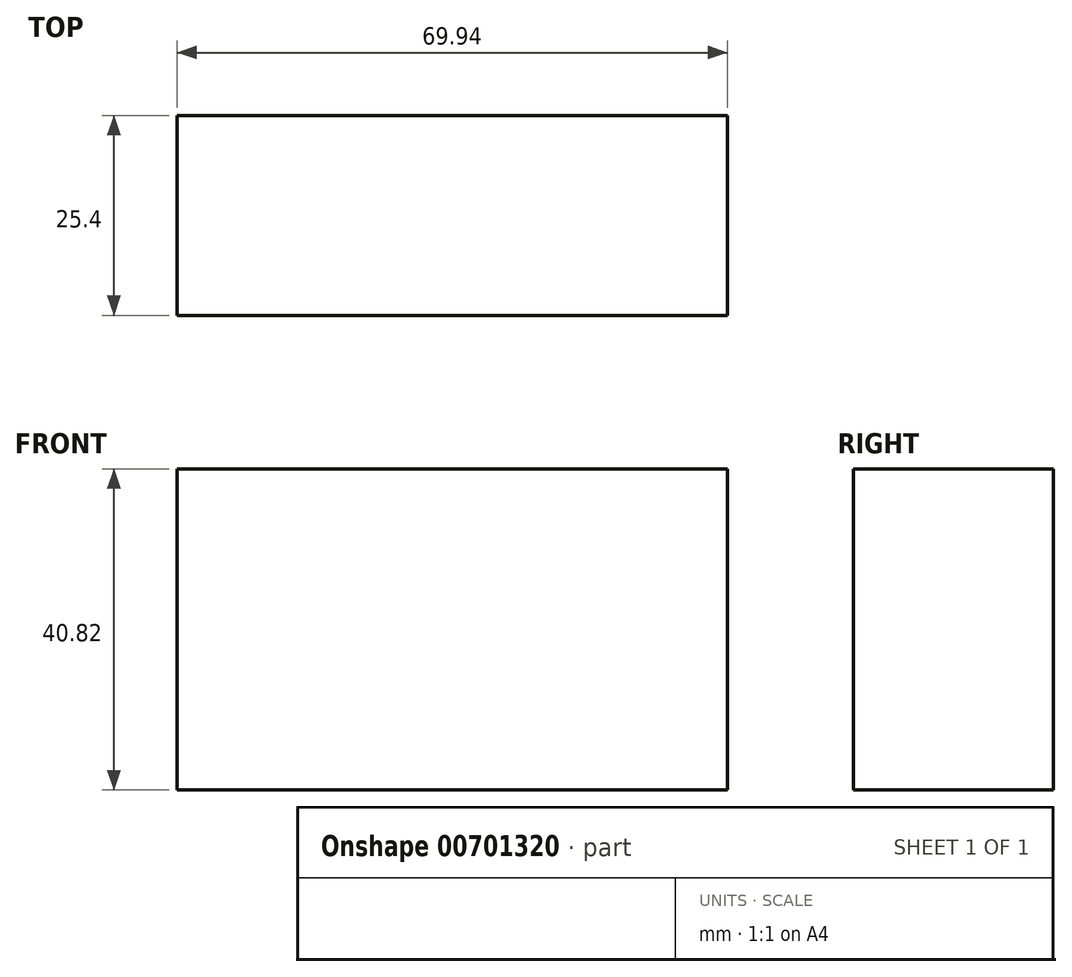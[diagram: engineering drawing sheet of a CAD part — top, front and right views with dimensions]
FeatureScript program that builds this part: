
annotation { "Feature Type Name" : "Feature", "Feature Type Description" : "" }
export const myFeature = defineFeature(function(context is Context, id is Id, definition is map)
    precondition{}
    {
        {
            var Q0;
            Q0=qCreatedBy(makeId("Front.planeOp"),FACE);
            var sketch = newSketch(context, id + "F0", { "sketchPlane" : qUnion([Q0])});
            skLineSegment(sketch, "E0.bottom", {"start": v(0, 0) * mm, "end": v(69.94, 0) * mm});
            skLineSegment(sketch, "E0.top", {"start": v(0, 40.82) * mm, "end": v(69.94, 40.82) * mm});
            skLineSegment(sketch, "E0.left", {"start": v(0, 0) * mm, "end": v(0, 40.82) * mm});
            skLineSegment(sketch, "E0.right", {"start": v(69.94, 0) * mm, "end": v(69.94, 40.82) * mm});
            skSolve(sketch);
        }
        {
            var Q0;
            Q0 = qSketchRegion(id + "F0", true);
            extrude(context, id + "F1", {"entities" : qUnion([Q0]), "depth" : 25.4 * mm, "offsetDistance" : 25.4 * mm});
        }
    });
